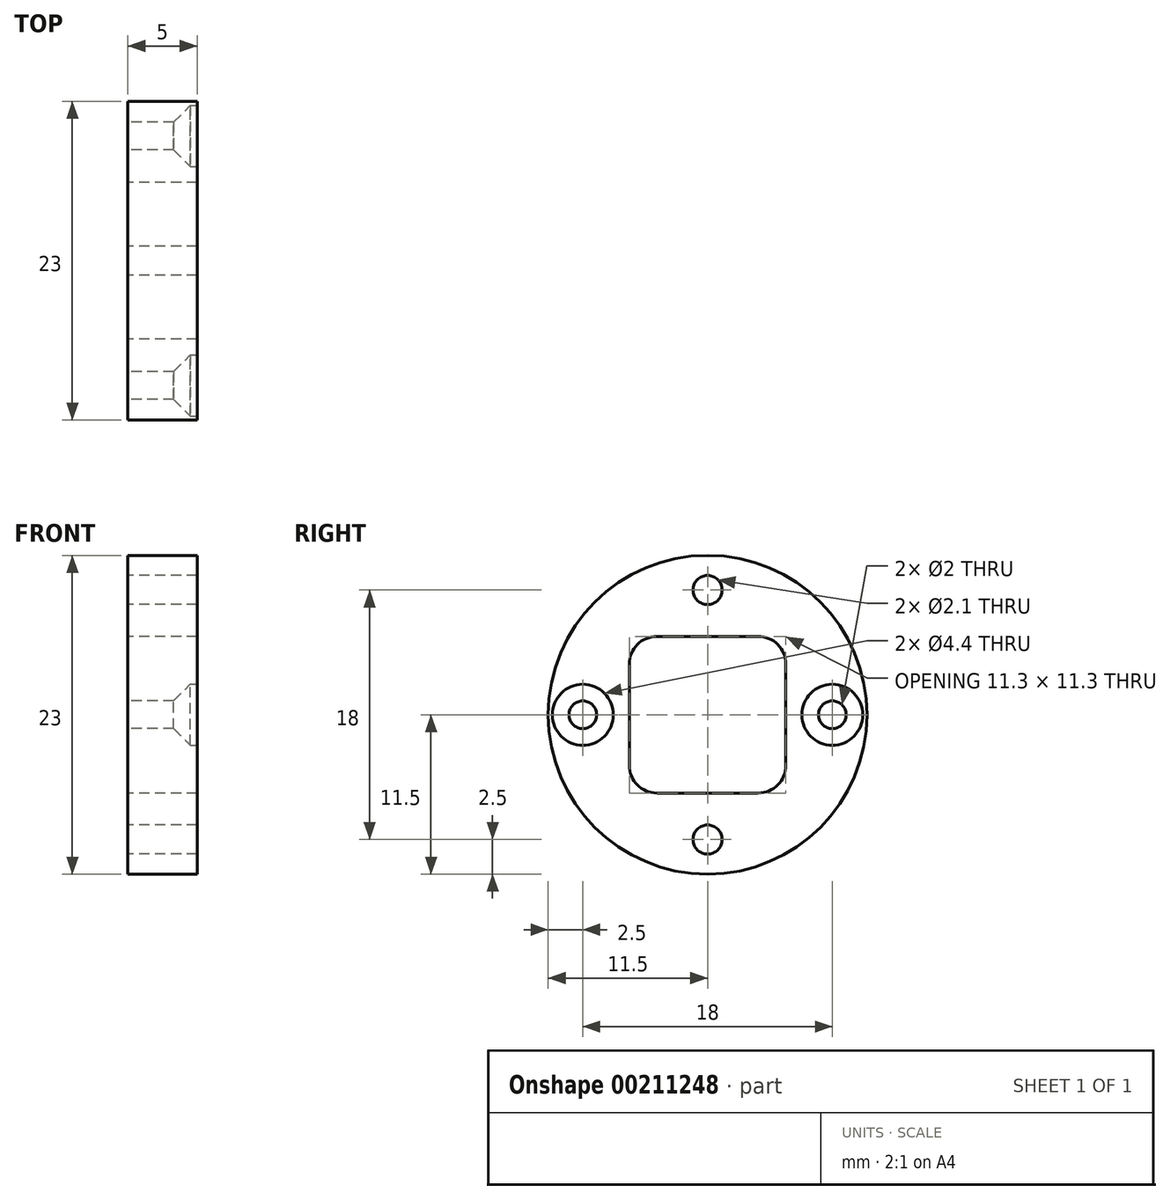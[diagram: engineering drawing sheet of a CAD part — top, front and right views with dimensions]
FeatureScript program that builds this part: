
annotation { "Feature Type Name" : "Feature", "Feature Type Description" : "" }
export const myFeature = defineFeature(function(context is Context, id is Id, definition is map)
    precondition{}
    {
        {
            var Q0;
            Q0=qCreatedBy(makeId("Right.planeOp"),FACE);
            var sketch = newSketch(context, id + "F0", { "sketchPlane" : qUnion([Q0])});
            skCircle(sketch, "E0", {"center": v(0, 0) * mm, "radius": 11.5 * mm});
            skCircle(sketch, "E1", {"center": v(0, 0) * mm, "radius": 9 * mm, "construction": true});
            skCircle(sketch, "E2", {"center": v(0, 9) * mm, "radius": 1.05 * mm});
            skCircle(sketch, "E3", {"center": v(9, 0) * mm, "radius": 1 * mm});
            skCircle(sketch, "E4", {"center": v(0, -9) * mm, "radius": 1.05 * mm});
            skCircle(sketch, "E5", {"center": v(-9, 0) * mm, "radius": 1 * mm});
            skLineSegment(sketch, "E6.bottom", {"start": v(-5.65, 5.65) * mm, "end": v(5.65, 5.65) * mm, "construction": true});
            skLineSegment(sketch, "E6.top", {"start": v(-5.65, -5.65) * mm, "end": v(5.65, -5.65) * mm, "construction": true});
            skLineSegment(sketch, "E6.left", {"start": v(-5.65, 5.65) * mm, "end": v(-5.65, -5.65) * mm, "construction": true});
            skLineSegment(sketch, "E6.right", {"start": v(5.65, 5.65) * mm, "end": v(5.65, -5.65) * mm, "construction": true});
            skLineSegment(sketch, "E7.bottom", {"start": v(-3.65, 3.65) * mm, "end": v(3.65, 3.65) * mm, "construction": true});
            skLineSegment(sketch, "E7.top", {"start": v(-3.65, -3.65) * mm, "end": v(3.65, -3.65) * mm, "construction": true});
            skLineSegment(sketch, "E7.left", {"start": v(-3.65, 3.65) * mm, "end": v(-3.65, -3.65) * mm, "construction": true});
            skLineSegment(sketch, "E7.right", {"start": v(3.65, 3.65) * mm, "end": v(3.65, -3.65) * mm, "construction": true});
            skArc(sketch, "E8", {"start": v(-3.65, 5.65) * mm, "mid": v(-5.06, 5.06) * mm, "end": v(-5.65, 3.65) * mm});
            skArc(sketch, "E9", {"start": v(-5.65, -3.65) * mm, "mid": v(-5.06, -5.06) * mm, "end": v(-3.65, -5.65) * mm});
            skArc(sketch, "E10", {"start": v(3.65, -5.65) * mm, "mid": v(5.06, -5.06) * mm, "end": v(5.65, -3.65) * mm});
            skArc(sketch, "E11", {"start": v(5.65, 3.65) * mm, "mid": v(5.06, 5.06) * mm, "end": v(3.65, 5.65) * mm});
            skLineSegment(sketch, "E12", {"start": v(-5.65, 3.65) * mm, "end": v(-5.65, -3.65) * mm});
            skLineSegment(sketch, "E13", {"start": v(-3.65, -5.65) * mm, "end": v(3.65, -5.65) * mm});
            skLineSegment(sketch, "E14", {"start": v(5.65, -3.65) * mm, "end": v(5.65, 3.65) * mm});
            skLineSegment(sketch, "E15", {"start": v(-3.65, 5.65) * mm, "end": v(3.65, 5.65) * mm});
            skLineSegment(sketch, "E16.bottom", {"start": v(5, -5) * mm, "end": v(-5, -5) * mm, "construction": true});
            skLineSegment(sketch, "E16.top", {"start": v(5, 5) * mm, "end": v(-5, 5) * mm, "construction": true});
            skLineSegment(sketch, "E16.left", {"start": v(5, -5) * mm, "end": v(5, 5) * mm, "construction": true});
            skLineSegment(sketch, "E16.right", {"start": v(-5, -5) * mm, "end": v(-5, 5) * mm, "construction": true});
            skSolve(sketch);
        }
        {
            var Q0;
            Q0 = qSketchRegion(id + "F0", true);
            extrude(context, id + "F1", {"entities" : qUnion([Q0]), "depth" : 5 * mm});
        }
        {
            var Q0;
            Q0=qCreatedBy(makeId("Front.planeOp"),FACE);
            cPlane(context, id + "F2", {"entities" : qUnion([Q0]), "cplaneType" : CPlaneType.OFFSET, "offset" : 9 * mm, "width" : 150 * mm, "height" : 150 * mm});
        }
        {
            var Q0;
            Q0=qCreatedBy(id+"F2.planeOp",FACE);
            var sketch = newSketch(context, id + "F3", { "sketchPlane" : qUnion([Q0])});
            skLineSegment(sketch, "E17", {"start": v(5, 0) * mm, "end": v(2.3, 0) * mm});
            skLineSegment(sketch, "E18", {"start": v(2.3, 0) * mm, "end": v(4.5, 2.2) * mm});
            skLineSegment(sketch, "E19", {"start": v(4.5, 2.2) * mm, "end": v(5, 2.2) * mm});
            skLineSegment(sketch, "E20", {"start": v(5, 2.2) * mm, "end": v(5, 0) * mm});
            skSolve(sketch);
        }
        {
            var Q0;
            Q0=qCreatedBy(id+"F2.planeOp",FACE);
            var sketch = newSketch(context, id + "F4", { "sketchPlane" : qUnion([Q0])});
            skLineSegment(sketch, "E21", {"start": v(-0.83, 0) * mm, "end": v(6.33, 0) * mm});
            skSolve(sketch);
        }
        {
            var Q0;
            Q0 = qSketchRegion(id + "F3", true);
            var Q1;
            Q1=sQuery(id+"F4.wireOp",EDGE,"E21");
            revolve(context, id + "F5", {"operationType" : NewBodyOperationType.REMOVE, "entities" : qUnion([Q0]), "axis" : qUnion([Q1]), "revolveType" : RevolveType.FULL, "oppositeDirection" : true});
        }
        {
            var Q0;
            Q0=qCreatedBy(makeId("Front.planeOp"),FACE);
            cPlane(context, id + "F6", {"entities" : qUnion([Q0]), "cplaneType" : CPlaneType.OFFSET, "offset" : 9 * mm, "oppositeDirection" : true, "width" : 150 * mm, "height" : 150 * mm});
        }
        {
            var Q0;
            Q0=qCreatedBy(id+"F6.planeOp",FACE);
            var sketch = newSketch(context, id + "F7", { "sketchPlane" : qUnion([Q0])});
            skLineSegment(sketch, "E22", {"start": v(2.3, 0) * mm, "end": v(5, 0) * mm});
            skLineSegment(sketch, "E23", {"start": v(5, 0) * mm, "end": v(5, 2.2) * mm});
            skLineSegment(sketch, "E24", {"start": v(5, 2.2) * mm, "end": v(4.5, 2.2) * mm});
            skLineSegment(sketch, "E25", {"start": v(4.5, 2.2) * mm, "end": v(2.3, 0) * mm});
            skSolve(sketch);
        }
        {
            var Q0;
            Q0 = qSketchRegion(id + "F7", true);
            var Q1;
            Q1=sQuery(id+"F7.wireOp",EDGE,"E22");
            revolve(context, id + "F8", {"operationType" : NewBodyOperationType.REMOVE, "entities" : qUnion([Q0]), "axis" : qUnion([Q1]), "revolveType" : RevolveType.FULL, "oppositeDirection" : true});
        }
    });
